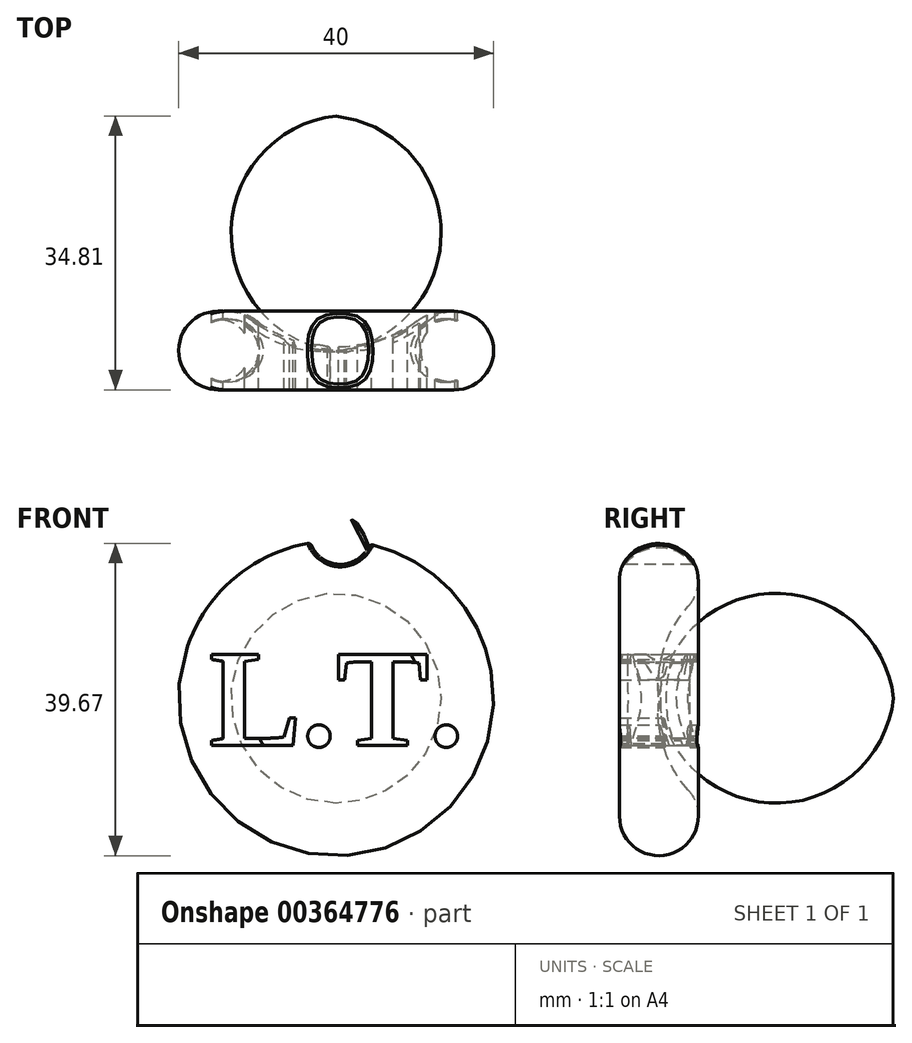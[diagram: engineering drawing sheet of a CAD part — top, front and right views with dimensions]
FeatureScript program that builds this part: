
annotation { "Feature Type Name" : "Feature", "Feature Type Description" : "" }
export const myFeature = defineFeature(function(context is Context, id is Id, definition is map)
    precondition{}
    {
        {
            var Q0;
            Q0=qCreatedBy(makeId("Top.planeOp"),FACE);
            var sketch = newSketch(context, id + "F0", { "sketchPlane" : qUnion([Q0])});
            skArc(sketch, "E0", {"start": v(-34, 12.46) * mm, "mid": v(-28.56, 9.35) * mm, "end": v(-22.33, 8.74) * mm});
            skArc(sketch, "E1", {"start": v(-34, 12.46) * mm, "mid": v(-42, 10.52) * mm, "end": v(-37.33, 3.74) * mm});
            skLineSegment(sketch, "E2", {"start": v(-37.33, 3.74) * mm, "end": v(-22.33, 3.74) * mm});
            skLineSegment(sketch, "E3", {"start": v(-22.33, 8.74) * mm, "end": v(-22.33, 3.74) * mm});
            skCircle(sketch, "E4", {"center": v(-37.33, 8.74) * mm, "radius": 4 * mm});
            skSolve(sketch);
        }
        {
            var Q0;
            Q0=makeQuery(id+"F0.imprint","IMPRINT",FACE,{"disambiguationData":[TD([[makeQuery(id+"F0.imprint","IMPRINT",EDGE,{"derivedFrom":sQuery(id+"F0.wireOp",EDGE,"E0")}),-1.0]])]});
            var Q1;
            Q1=sQuery(id+"F0.wireOp",EDGE,"E3");
            revolve(context, id + "F1", {"entities" : qUnion([Q0]), "axis" : qUnion([Q1]), "revolveType" : RevolveType.FULL});
        }
        {
            var Q0;
            Q0=qCreatedBy(makeId("Front.planeOp"),FACE);
            cPlane(context, id + "F2", {"entities" : qUnion([Q0]), "cplaneType" : CPlaneType.OFFSET, "offset" : 17.3 * mm, "oppositeDirection" : true, "width" : 150 * mm, "height" : 150 * mm});
        }
        {
            var Q0;
            Q0=qCreatedBy(id+"F2.planeOp",FACE);
            var sketch = newSketch(context, id + "F3", { "sketchPlane" : qUnion([Q0])});
            skText(sketch, "E5", { "text": "L.T.", "fontName": "Tinos-Bold.ttf"});
            const initialGuessF3  = {"E5": [-0.03848, -0.006, 1, 0, 0.0127]};
            skSetInitialGuess(sketch, initialGuessF3);
            skSolve(sketch);
        }
        {
            var Q0;
            Q0 = qSketchRegion(id + "F3", true);
            extrude(context, id + "F4", {"entities" : qUnion([Q0]), "operationType" : NewBodyOperationType.REMOVE, "endBound" : BoundingType.THROUGH_ALL, "depth" : 10 * mm});
        }
        {
            var Q0;
            Q0=makeQuery(id+"F0.imprint","IMPRINT",FACE,{"disambiguationData":[TD([[makeQuery(id+"F0.imprint","IMPRINT",EDGE,{"derivedFrom":sQuery(id+"F0.wireOp",EDGE,"E4")}),1.0]])]});
            var Q1;
            Q1=sQuery(id+"F0.wireOp",EDGE,"E4");
            var Q2;
            Q2=sQuery(id+"F0.wireOp",EDGE,"E3");
            var Q3;
            Q3=sQuery(id+"F0.wireOp",EDGE,"E3");
            revolve(context, id + "F5", {"operationType" : NewBodyOperationType.ADD, "entities" : qUnion([Q0]), "surfaceEntities" : qUnion([Q1, Q2]), "axis" : qUnion([Q3]), "revolveType" : RevolveType.FULL});
        }
        {
            var Q0;
            Q0=makeQuery(id+"F4.boolean.opBoolean","SPLIT",FACE,{"disambiguationData":[TD([makeQuery(id+"F4.opExtrude","SWEPT_FACE",FACE,{"disambiguationData":[OSD([sQuery(id+"F3.wireOp",EDGE,"E5.sketch_text.stroke-0")])]})])],"derivedFrom":makeQuery(id+"F1.opRevolve","SWEPT_FACE",FACE,{"disambiguationData":[OSD([sQuery(id+"F0.wireOp",EDGE,"E2")])]})});
            var sketch = newSketch(context, id + "F6", { "sketchPlane" : qUnion([Q0])});
            skCircle(sketch, "E6", {"center": v(-21.78, 21) * mm, "radius": 4 * mm});
            skSolve(sketch);
        }
        {
            var Q0;
            Q0 = qSketchRegion(id + "F6", true);
            extrude(context, id + "F7", {"entities" : qUnion([Q0]), "operationType" : NewBodyOperationType.REMOVE, "oppositeDirection" : true, "depth" : 25 * mm});
        }
        {
            var Q0;
            Q0=makeQuery(id+"F7.boolean.opBoolean","INTERSECT",EDGE,{"derivedFrom":[makeQuery(id+"F4.boolean.opBoolean","SPLIT",FACE,{"disambiguationData":[TD([makeQuery(id+"F1.opRevolve","SWEPT_FACE",FACE,{"disambiguationData":[OSD([sQuery(id+"F0.wireOp",EDGE,"E2")])]})])],"derivedFrom":makeQuery(id+"F1.opRevolve","SWEPT_FACE",FACE,{"disambiguationData":[OSD([sQuery(id+"F0.wireOp",EDGE,"E1")])]})}),makeQuery(id+"F7.opExtrude","SWEPT_FACE",FACE,{"disambiguationData":[OSD([sQuery(id+"F6.wireOp",EDGE,"E6")])]})]});
            fillet(context, id + "F8", {"entities" : qUnion([Q0]), "radius" : .5 * mm, "tangentPropagation" : true, "allowEdgeOverflow" : false});
        }
    });
